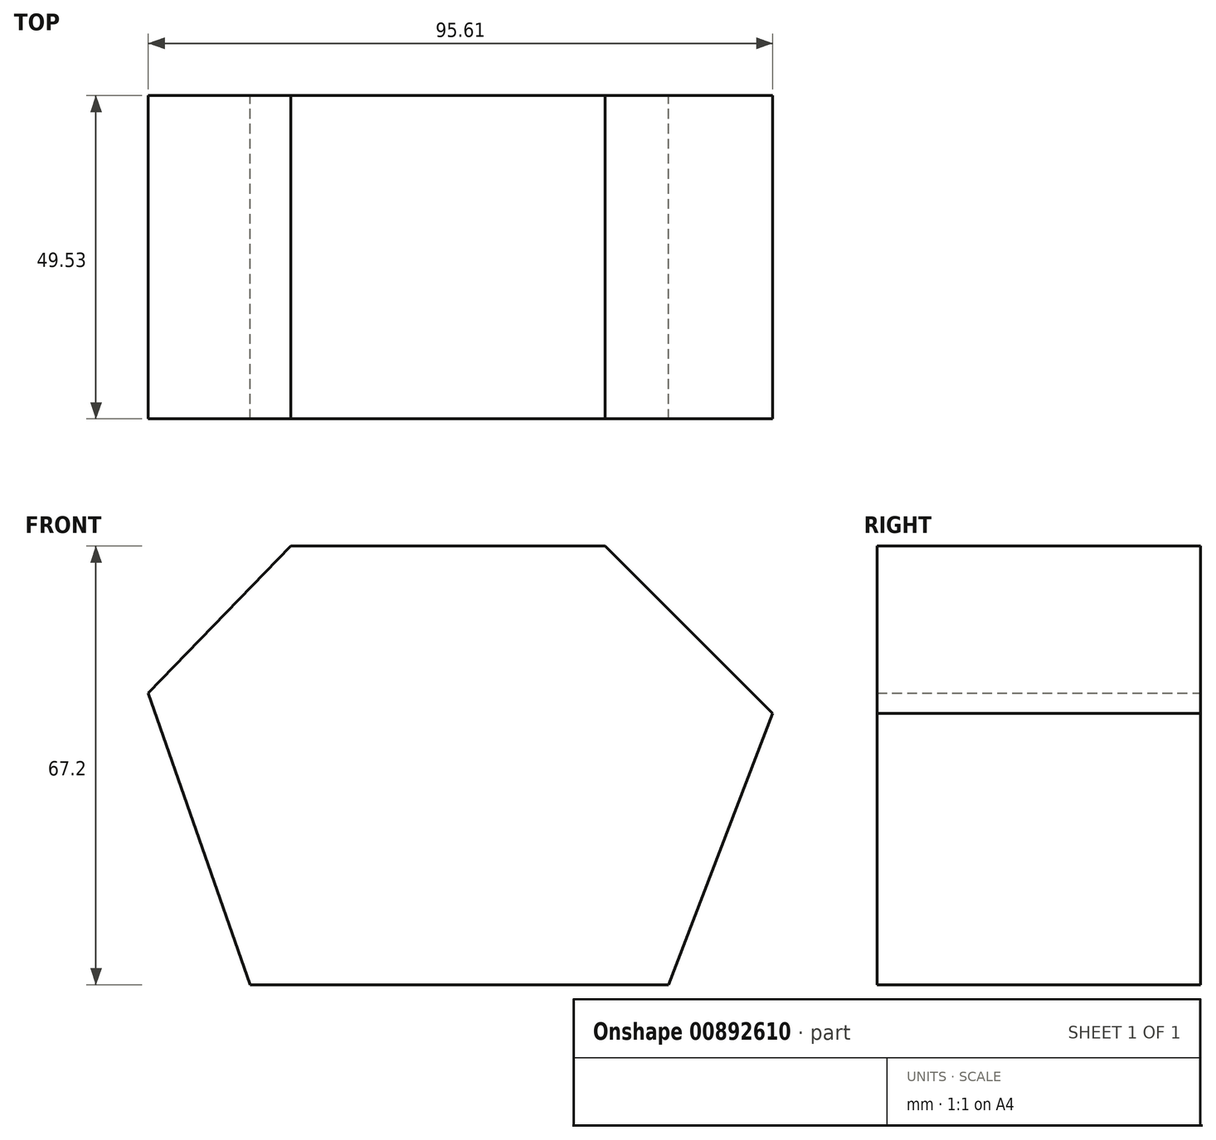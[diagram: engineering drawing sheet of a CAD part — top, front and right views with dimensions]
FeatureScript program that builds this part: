
annotation { "Feature Type Name" : "Feature", "Feature Type Description" : "" }
export const myFeature = defineFeature(function(context is Context, id is Id, definition is map)
    precondition{}
    {
        {
            var Q0;
            Q0=qCreatedBy(makeId("Front.planeOp"),FACE);
            var sketch = newSketch(context, id + "F0", { "sketchPlane" : qUnion([Q0])});
            skLineSegment(sketch, "E0", {"start": v(-33.8, 30.03) * mm, "end": v(-18.21, -14.66) * mm});
            skLineSegment(sketch, "E1", {"start": v(45.87, -14.66) * mm, "end": v(-18.21, -14.66) * mm});
            skLineSegment(sketch, "E2", {"start": v(45.87, -14.66) * mm, "end": v(61.8, 26.91) * mm});
            skLineSegment(sketch, "E3", {"start": v(61.8, 26.91) * mm, "end": v(36.17, 52.54) * mm});
            skLineSegment(sketch, "E4", {"start": v(36.17, 52.54) * mm, "end": v(-11.98, 52.54) * mm});
            skLineSegment(sketch, "E5", {"start": v(-11.98, 52.54) * mm, "end": v(-33.8, 30.03) * mm});
            skSolve(sketch);
        }
        {
            var Q0;
            Q0=makeQuery(id+"F0.imprint","IMPRINT",FACE,{"disambiguationData":[TD([[makeQuery(id+"F0.imprint","IMPRINT",EDGE,{"derivedFrom":sQuery(id+"F0.wireOp",EDGE,"E0")}),1.0]])]});
            extrude(context, id + "F1", {"entities" : qUnion([Q0]), "depth" : 49.53 * mm, "offsetDistance" : 25.4 * mm});
        }
    });
